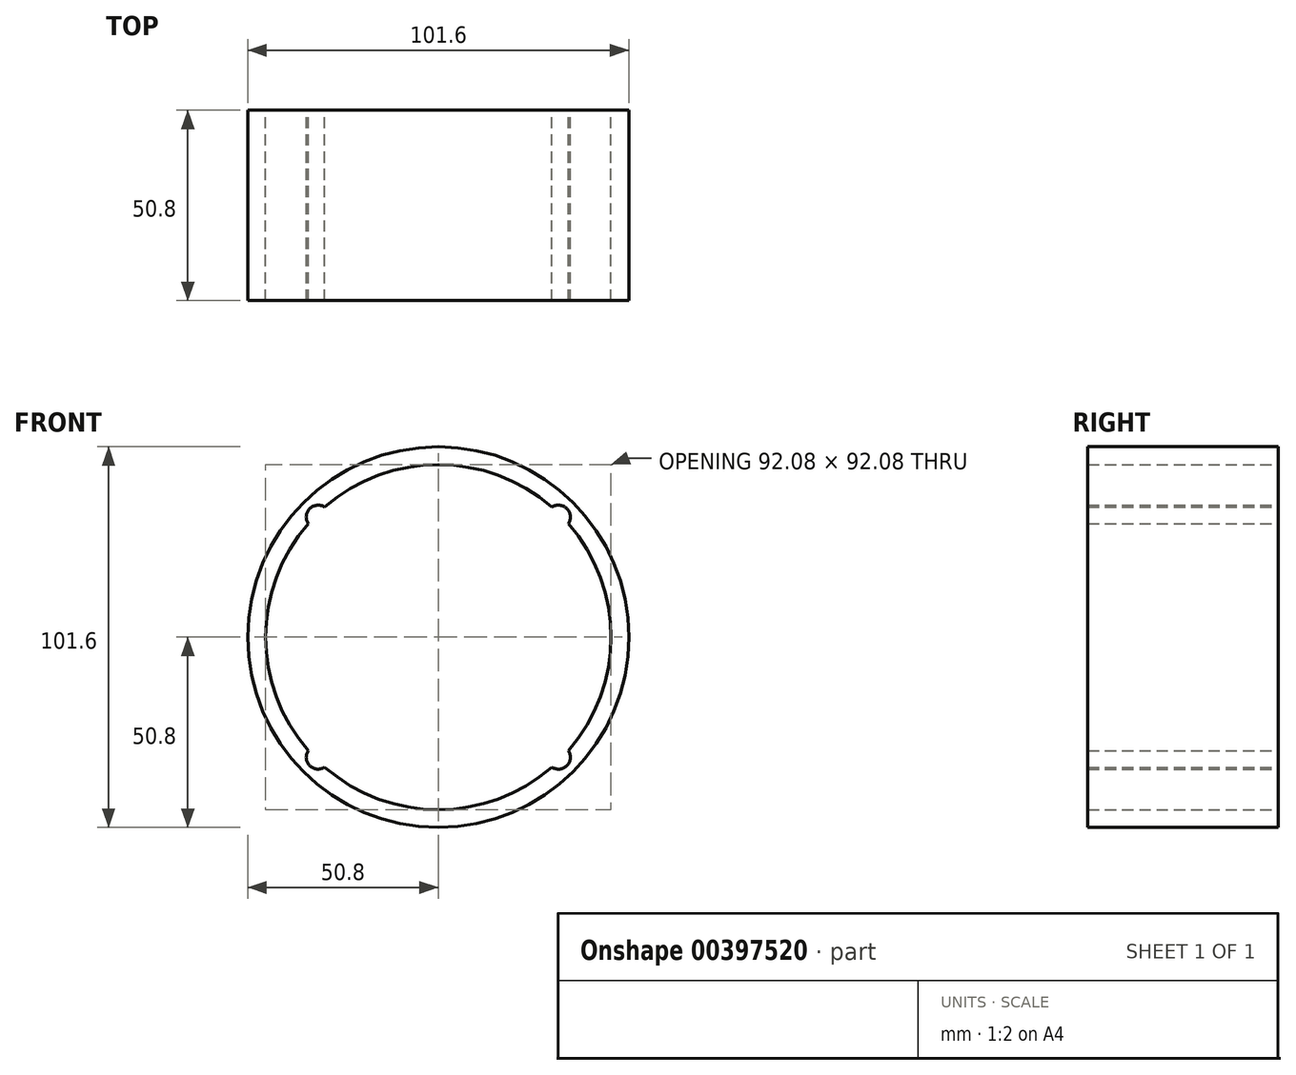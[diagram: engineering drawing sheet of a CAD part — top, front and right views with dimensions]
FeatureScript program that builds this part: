
annotation { "Feature Type Name" : "Feature", "Feature Type Description" : "" }
export const myFeature = defineFeature(function(context is Context, id is Id, definition is map)
    precondition{}
    {
        {
            var Q0;
            Q0=qCreatedBy(makeId("Front.planeOp"),FACE);
            var sketch = newSketch(context, id + "F0", { "sketchPlane" : qUnion([Q0])});
            skPoint(sketch, "E0.middle", {"position": v(0, 0) * mm});
            skArc(sketch, "E1", {"start": v(-30.28, 34.68) * mm, "mid": v(-34.3, 34.3) * mm, "end": v(-34.68, 30.28) * mm});
            skArc(sketch, "E2", {"start": v(34.68, 30.28) * mm, "mid": v(34.3, 34.3) * mm, "end": v(30.28, 34.68) * mm});
            skArc(sketch, "E3", {"start": v(-34.68, -30.28) * mm, "mid": v(-34.3, -34.3) * mm, "end": v(-30.28, -34.68) * mm});
            skArc(sketch, "E4", {"start": v(30.28, -34.68) * mm, "mid": v(34.29, -34.3) * mm, "end": v(34.68, -30.28) * mm});
            skCircle(sketch, "E5", {"center": v(0, 0) * mm, "radius": 50.8 * mm});
            skArc(sketch, "E6", {"start": v(30.28, 34.68) * mm, "mid": v(0, 46.04) * mm, "end": v(-30.28, 34.68) * mm});
            skArc(sketch, "E7.trimOffspring", {"start": v(-34.68, 30.28) * mm, "mid": v(-46.04, 0) * mm, "end": v(-34.68, -30.28) * mm});
            skArc(sketch, "E8.trimOffspring", {"start": v(-30.28, -34.68) * mm, "mid": v(0, -46.04) * mm, "end": v(30.28, -34.68) * mm});
            skArc(sketch, "E9.trimOffspring", {"start": v(34.68, -30.28) * mm, "mid": v(46.04, 0) * mm, "end": v(34.68, 30.28) * mm});
            skSolve(sketch);
        }
        {
            var Q0;
            Q0=makeQuery(id+"F0.imprint","IMPRINT",FACE,{"disambiguationData":[TD([[makeQuery(id+"F0.imprint","IMPRINT",EDGE,{"derivedFrom":sQuery(id+"F0.wireOp",EDGE,"E1")}),-1.0]])]});
            extrude(context, id + "F1", {"entities" : qUnion([Q0]), "depth" : 50.8 * mm});
        }
    });
